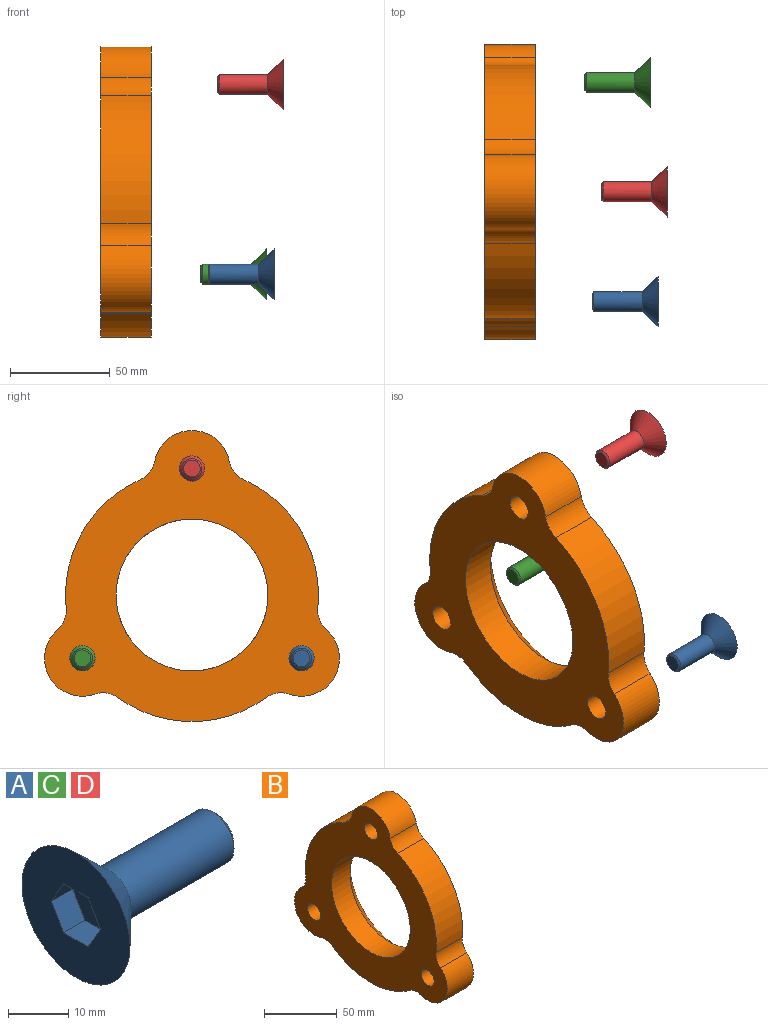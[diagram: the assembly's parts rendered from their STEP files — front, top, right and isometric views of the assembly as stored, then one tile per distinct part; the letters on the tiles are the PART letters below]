
ASSEMBLY  parts=4 mates=3
PART A: 12 faces, bbox 33x25.5x25.5 mm
  f0: plane 25.45x25.45mm, normal (-1,0,0), area 422.1mm2, adj f3,f4,f5,f6,f7,f8,f9
  f1: plane 8.4x8.4mm, normal (1,0,0), area 55.4mm2, adj f11
  f2: cylinder r=5mm len=24.2mm, axis (1,0,0), area 760.3mm2, adj f3,f11
  f3: cone r=12.73mm half-angle=44deg, axis (-1,0,0), area 619.3mm2, adj f0,f2
  f4: plane 5x5mm, normal (0,-0.87,-0.5), area 28.9mm2, adj f0,f5,f9,f10
  f5: plane 5x5mm, normal (0,-0.87,0.5), area 28.9mm2, adj f0,f4,f6,f10
  f6: plane 5.77x5mm, normal (0,0,1), area 28.9mm2, adj f0,f5,f7,f10
  f7: plane 5x5mm, normal (0,0.87,0.5), area 28.9mm2, adj f0,f6,f8,f10
  f8: plane 5x5mm, normal (0,0.87,-0.5), area 28.9mm2, adj f0,f7,f9,f10
  f9: plane 5.77x5mm, normal (0,0,-1), area 28.9mm2, adj f0,f4,f8,f10
  f10: plane 11.55x10mm, normal (-1,0,0), area 86.6mm2, adj f4,f5,f6,f7,f8,f9
  f11: cone r=4.2mm half-angle=45deg, axis (-1,0,0), area 32.7mm2, adj f1,f2
PART B: 22 faces, bbox 25.4x148.1x146.1 mm
  f0: cylinder r=63.5mm len=64.42mm, axis (-1,0,0), area 2018.6mm2, adj f7,f8,f13,f18
  f1: cylinder r=19.05mm len=33.44mm, axis (-1,0,0), area 1335.1mm2, adj f7,f8,f13,f14
  f2: cylinder r=63.5mm len=74.39mm, axis (-1,0,0), area 2018.6mm2, adj f7,f8,f14,f15
  f3: cylinder r=19.05mm len=33.44mm, axis (-1,0,0), area 1335.1mm2, adj f7,f8,f15,f16
  f4: cylinder r=63.5mm len=64.42mm, axis (-1,0,0), area 2018.6mm2, adj f7,f8,f16,f17
  f5: cylinder r=19.05mm len=37.41mm, axis (-1,0,0), area 1335.1mm2, adj f7,f8,f17,f18
  f6: cylinder r=38.1mm len=76.2mm, axis (-1,0,0), area 4256.3mm2, adj f8,f9
  f7: plane 148.09x146.05mm, normal (1,0,0), area 6748mm2, adj f0,f1,f2,f3,f4,f5,f9,f13
  f8: plane 148.09x146.05mm, normal (-1,0,0), area 9605.8mm2, adj f0,f1,f2,f3,f4,f5,f6,f10
  f9: cone r=38.1mm half-angle=45deg, axis (1,0,0), area 2837.7mm2, adj f6,f7
  f10: cylinder r=6.35mm len=20.32mm, axis (1,0,0), area 810.7mm2, adj f8,f19
  f11: cylinder r=6.35mm len=20.32mm, axis (1,0,0), area 810.7mm2, adj f8,f20
  f12: cylinder r=6.35mm len=20.32mm, axis (1,0,0), area 810.7mm2, adj f8,f21
  f13: cylinder r=12.7mm len=25.4mm, axis (1,0,0), area 309.1mm2, adj f0,f1,f7,f8
  f14: cylinder r=12.7mm len=25.4mm, axis (1,0,0), area 309.1mm2, adj f1,f2,f7,f8
  f15: cylinder r=12.7mm len=25.4mm, axis (1,0,0), area 309.1mm2, adj f2,f3,f7,f8
  f16: cylinder r=12.7mm len=25.4mm, axis (1,0,0), area 309.1mm2, adj f3,f4,f7,f8
  f17: cylinder r=12.7mm len=25.4mm, axis (1,0,0), area 309.1mm2, adj f4,f5,f7,f8
  f18: cylinder r=12.7mm len=25.4mm, axis (1,0,0), area 309.1mm2, adj f0,f5,f7,f8
  f19: cone r=6.35mm half-angle=45deg, axis (1,0,0), area 401.3mm2, adj f7,f10
  f20: cone r=6.35mm half-angle=45deg, axis (1,0,0), area 401.3mm2, adj f7,f11
  f21: cone r=6.35mm half-angle=45deg, axis (1,0,0), area 401.3mm2, adj f7,f12
PART C: same geometry as A
PART D: same geometry as A
PLACE A rot(axis=(0,-0.52,0.86),180deg) t=(87,-54.99,-31.75)mm
PLACE B at identity fixed
PLACE C rot(axis=(0,-1,0.02),180deg) t=(83.31,54.99,-31.75)mm
PLACE D rot(axis=(0,-0.94,-0.35),180deg) t=(91.66,0,63.5)mm
MATE cylindrical D.f2 <-> B.f5  axis (-1,0,0) through (71.56,0,63.5)mm
MATE cylindrical C.f2 <-> B.f3  axis (-1,0,0) through (75.31,54.99,-31.75)mm
MATE cylindrical A.f2 <-> B.f1  axis (-1,0,0) through (66.9,-54.99,-31.75)mm
